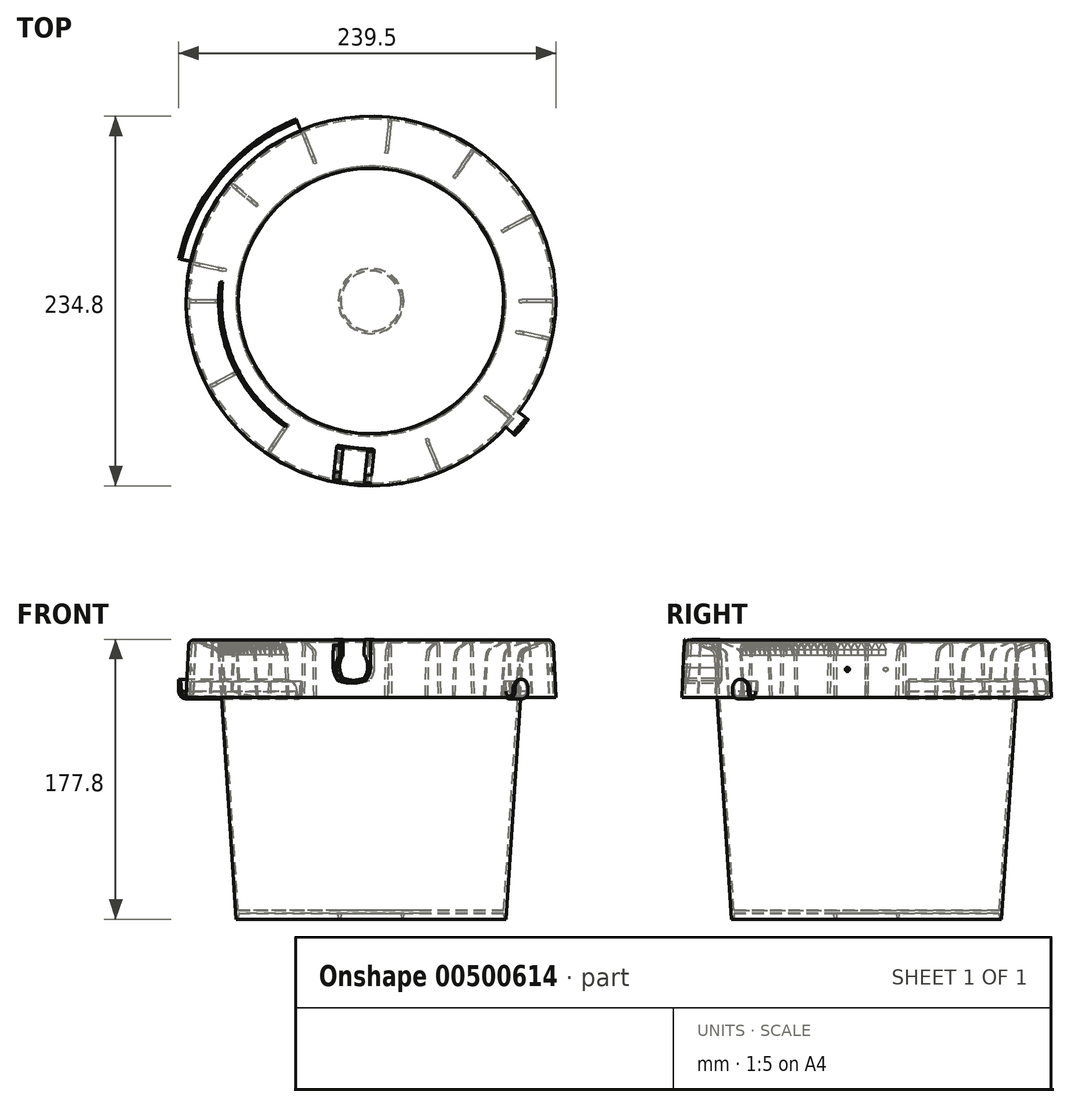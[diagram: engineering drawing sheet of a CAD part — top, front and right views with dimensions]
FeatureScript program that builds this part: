
annotation { "Feature Type Name" : "Feature", "Feature Type Description" : "" }
export const myFeature = defineFeature(function(context is Context, id is Id, definition is map)
    precondition{}
    {
        {
            var Q0;
            Q0=qCreatedBy(makeId("Front.planeOp"),FACE);
            var sketch = newSketch(context, id + "F0", { "sketchPlane" : qUnion([Q0])});
            skLineSegment(sketch, "E0", {"start": v(20.57, 0) * mm, "end": v(19.3, 0) * mm});
            skLineSegment(sketch, "E1", {"start": v(19.3, 0) * mm, "end": v(19.05, 3.81) * mm});
            skLineSegment(sketch, "E2", {"start": v(20.83, 3.81) * mm, "end": v(20.57, 0) * mm});
            skLineSegment(sketch, "E3", {"start": v(0, 0) * mm, "end": v(0, 3.81) * mm});
            skLineSegment(sketch, "E4", {"start": v(0, 3.81) * mm, "end": v(19.05, 3.81) * mm});
            skLineSegment(sketch, "E5", {"start": v(0, 3.81) * mm, "end": v(0, 5.59) * mm});
            skLineSegment(sketch, "E6", {"start": v(0, 5.59) * mm, "end": v(84.3, 5.59) * mm});
            skLineSegment(sketch, "E7", {"start": v(20.83, 3.81) * mm, "end": v(84.3, 3.8) * mm});
            skLineSegment(sketch, "E8", {"start": v(0, 0) * mm, "end": v(0, 179.07) * mm});
            skLineSegment(sketch, "E9", {"start": v(0, 0) * mm, "end": v(0, 171.45) * mm});
            skLineSegment(sketch, "E10", {"start": v(115.62, 140.97) * mm, "end": v(117.4, 140.97) * mm});
            skArc(sketch, "E11", {"start": v(114.08, 174.01) * mm, "mid": v(113.25, 175.47) * mm, "end": v(111.59, 175.66) * mm});
            skLineSegment(sketch, "E12", {"start": v(114.08, 174.01) * mm, "end": v(115.62, 140.97) * mm});
            skLineSegment(sketch, "E13", {"start": v(111.59, 175.66) * mm, "end": v(110.96, 177.33) * mm});
            skLineSegment(sketch, "E14", {"start": v(114.08, 174.01) * mm, "end": v(115.86, 174.1) * mm});
            skLineSegment(sketch, "E15", {"start": v(115.86, 174.1) * mm, "end": v(117.4, 140.97) * mm});
            skArc(sketch, "E16", {"start": v(99.32, 171.08) * mm, "mid": v(97.55, 169.74) * mm, "end": v(96.78, 167.65) * mm});
            skLineSegment(sketch, "E17", {"start": v(96.78, 167.65) * mm, "end": v(85.73, 0) * mm});
            skLineSegment(sketch, "E18", {"start": v(99.32, 171.08) * mm, "end": v(111.59, 175.66) * mm});
            skLineSegment(sketch, "E19", {"start": v(96.78, 167.65) * mm, "end": v(95, 167.77) * mm});
            skLineSegment(sketch, "E20", {"start": v(99.32, 171.08) * mm, "end": v(98.7, 172.74) * mm});
            skLineSegment(sketch, "E21", {"start": v(110.96, 177.33) * mm, "end": v(98.7, 172.74) * mm});
            skLineSegment(sketch, "E22", {"start": v(95, 167.77) * mm, "end": v(84.3, 5.59) * mm});
            skArc(sketch, "E23", {"start": v(98.7, 172.74) * mm, "mid": v(96.12, 170.8) * mm, "end": v(95, 167.77) * mm});
            skLineSegment(sketch, "E24", {"start": v(84.3, 3.8) * mm, "end": v(84.18, 3.8) * mm, "construction": true});
            skLineSegment(sketch, "E25", {"start": v(85.73, 0) * mm, "end": v(84.38, 0) * mm});
            skLineSegment(sketch, "E26", {"start": v(84.18, 3.8) * mm, "end": v(84.38, 0) * mm});
            skLineSegment(sketch, "E27", {"start": v(117.4, 140.97) * mm, "end": v(0, 140.97) * mm, "construction": true});
            skLineSegment(sketch, "E28", {"start": v(95, 167.77) * mm, "end": v(0, 167.77) * mm, "construction": true});
            skLineSegment(sketch, "E29", {"start": v(0, 177.33) * mm, "end": v(0, 179.1) * mm});
            skLineSegment(sketch, "E30", {"start": v(116.18, 167.13) * mm, "end": v(117.96, 167.13) * mm, "construction": true});
            skLineSegment(sketch, "E31", {"start": v(116.18, 167.13) * mm, "end": v(117.96, 167.13) * mm});
            skPoint(sketch, "E32.orphan", {"position": v(120.3, 167.13) * mm});
            skPoint(sketch, "E33.orphan", {"position": v(115.62, 167.13) * mm});
            skLineSegment(sketch, "E34", {"start": v(117.63, 174.1) * mm, "end": v(117.96, 167.13) * mm, "construction": true});
            skLineSegment(sketch, "E35", {"start": v(117.96, 167.13) * mm, "end": v(117.63, 174.1) * mm});
            skPoint(sketch, "E36.start.orphan", {"position": v(115.7, 177.55) * mm});
            skArc(sketch, "E37", {"start": v(117.63, 174.1) * mm, "mid": v(115.95, 177.7) * mm, "end": v(112.23, 179.07) * mm});
            skArc(sketch, "E38", {"start": v(115.86, 174.1) * mm, "mid": v(114.23, 176.96) * mm, "end": v(110.96, 177.33) * mm});
            skSolve(sketch);
        }
        {
            var Q0;
            Q0=qSketchRegion(id+"F0",true);
            var Q1;
            Q1=sQuery(id+"F0.wireOp",EDGE,"E9");
            revolve(context, id + "F1", {"entities" : qUnion([Q0]), "axis" : qUnion([Q1]), "revolveType" : RevolveType.FULL});
        }
        {
            var Q0;
            Q0=qCreatedBy(makeId("Front.planeOp"),FACE);
            var sketch = newSketch(context, id + "F2", { "sketchPlane" : qUnion([Q0])});
            skLineSegment(sketch, "E39", {"start": v(0, 0) * mm, "end": v(0, 3.8) * mm});
            skLineSegment(sketch, "E40", {"start": v(0, 3.8) * mm, "end": v(0, 5.59) * mm});
            skLineSegment(sketch, "E41", {"start": v(0, 0) * mm, "end": v(0, 179.07) * mm});
            skLineSegment(sketch, "E42", {"start": v(0, 0) * mm, "end": v(0, 171.45) * mm});
            skLineSegment(sketch, "E43", {"start": v(0, 179.07) * mm, "end": v(157.98, 179.07) * mm, "construction": true});
            skLineSegment(sketch, "E44", {"start": v(0, 179.07) * mm, "end": v(115.62, 179.07) * mm, "construction": true});
            skLineSegment(sketch, "E45", {"start": v(114.08, 174.01) * mm, "end": v(115.62, 140.97) * mm});
            skLineSegment(sketch, "E46", {"start": v(0, 177.55) * mm, "end": v(129.4, 177.55) * mm, "construction": true});
            skLineSegment(sketch, "E47", {"start": v(111.31, 176.37) * mm, "end": v(99.06, 171.79) * mm});
            skLineSegment(sketch, "E48", {"start": v(94.26, 140.97) * mm, "end": v(96.02, 167.65) * mm});
            skArc(sketch, "E49", {"start": v(99.06, 171.79) * mm, "mid": v(96.93, 170.16) * mm, "end": v(96.02, 167.65) * mm});
            skArc(sketch, "E50", {"start": v(114.08, 174.01) * mm, "mid": v(113.2, 175.8) * mm, "end": v(111.31, 176.37) * mm});
            skLineSegment(sketch, "E51", {"start": v(115.62, 140.97) * mm, "end": v(94.26, 140.97) * mm});
            skSolve(sketch);
        }
        {
            var Q0;
            Q0=makeQuery(id+"F2.imprint","IMPRINT",FACE,{"disambiguationData":[TD([[makeQuery(id+"F2.imprint","IMPRINT",EDGE,{"derivedFrom":sQuery(id+"F2.wireOp",EDGE,"E45")}),-1.0]])]});
            extrude(context, id + "F3", {"entities" : qUnion([Q0]), "endBound" : BoundingType.SYMMETRIC, "depth" : 1.78 * mm});
        }
        {
            var Q0;
            Q0=makeQuery(id+"F3.opExtrude","SWEPT_BODY",BODY,{"disambiguationData":[OSD([sQuery(id+"F2.wireOp",EDGE,"E45"),sQuery(id+"F2.wireOp",EDGE,"E47"),sQuery(id+"F2.wireOp",EDGE,"E48"),sQuery(id+"F2.wireOp",EDGE,"E49"),sQuery(id+"F2.wireOp",EDGE,"E50"),sQuery(id+"F2.wireOp",EDGE,"E51")])]});
            var Q1;
            Q1=makeQuery(id+"F1.opRevolve","SWEPT_FACE",FACE,{"disambiguationData":[OSD([sQuery(id+"F0.wireOp",EDGE,"E15")])]});
            circularPattern(context, id + "F4", {"entities" : qUnion([Q0]), "axis" : qUnion([Q1]), "angle" : 12 * degree, "instanceCount" : 2, "equalSpace" : true});
        }
        {
            var Q0;
            Q0=makeQuery(id+"F3.opExtrude","SWEPT_BODY",BODY,{"disambiguationData":[OSD([sQuery(id+"F2.wireOp",EDGE,"E45"),sQuery(id+"F2.wireOp",EDGE,"E47"),sQuery(id+"F2.wireOp",EDGE,"E48"),sQuery(id+"F2.wireOp",EDGE,"E49"),sQuery(id+"F2.wireOp",EDGE,"E50"),sQuery(id+"F2.wireOp",EDGE,"E51")])]});
            var Q1;
            Q1=makeQuery(id+"F1.opRevolve","SWEPT_FACE",FACE,{"disambiguationData":[OSD([sQuery(id+"F0.wireOp",EDGE,"E12")])]});
            circularPattern(context, id + "F5", {"entities" : qUnion([Q0]), "axis" : qUnion([Q1]), "angle" : 28 * degree, "instanceCount" : 2, "equalSpace" : true});
        }
        {
            var Q0;
            Q0=makeQuery(id+"F3.opExtrude","SWEPT_BODY",BODY,{"disambiguationData":[OSD([sQuery(id+"F2.wireOp",EDGE,"E45"),sQuery(id+"F2.wireOp",EDGE,"E47"),sQuery(id+"F2.wireOp",EDGE,"E48"),sQuery(id+"F2.wireOp",EDGE,"E49"),sQuery(id+"F2.wireOp",EDGE,"E50"),sQuery(id+"F2.wireOp",EDGE,"E51")])]});
            var Q1;
            Q1=makeQuery(id+"F1.opRevolve","SWEPT_FACE",FACE,{"disambiguationData":[OSD([sQuery(id+"F0.wireOp",EDGE,"E12")])]});
            circularPattern(context, id + "F6", {"entities" : qUnion([Q0]), "axis" : qUnion([Q1]), "angle" : 56 * degree, "instanceCount" : 2, "equalSpace" : true});
        }
        {
            var Q0;
            Q0=makeQuery(id+"F3.opExtrude","SWEPT_BODY",BODY,{"disambiguationData":[OSD([sQuery(id+"F2.wireOp",EDGE,"E45"),sQuery(id+"F2.wireOp",EDGE,"E47"),sQuery(id+"F2.wireOp",EDGE,"E48"),sQuery(id+"F2.wireOp",EDGE,"E49"),sQuery(id+"F2.wireOp",EDGE,"E50"),sQuery(id+"F2.wireOp",EDGE,"E51")])]});
            var Q1;
            Q1=makeQuery(id+"F1.opRevolve","SWEPT_FACE",FACE,{"disambiguationData":[OSD([sQuery(id+"F0.wireOp",EDGE,"E12")])]});
            circularPattern(context, id + "F7", {"entities" : qUnion([Q0]), "axis" : qUnion([Q1]), "angle" : 84 * degree, "instanceCount" : 2, "equalSpace" : true});
        }
        {
            var Q0;
            Q0=makeQuery(id+"F1.opRevolve","SWEPT_BODY",BODY,{"disambiguationData":[OSD([sQuery(id+"F0.wireOp",EDGE,"E0"),sQuery(id+"F0.wireOp",EDGE,"E1"),sQuery(id+"F0.wireOp",EDGE,"E2"),sQuery(id+"F0.wireOp",EDGE,"E4"),sQuery(id+"F0.wireOp",EDGE,"E6"),sQuery(id+"F0.wireOp",EDGE,"E7"),sQuery(id+"F0.wireOp",EDGE,"E9"),sQuery(id+"F0.wireOp",EDGE,"E10"),sQuery(id+"F0.wireOp",EDGE,"E11"),sQuery(id+"F0.wireOp",EDGE,"E12"),sQuery(id+"F0.wireOp",EDGE,"E15"),sQuery(id+"F0.wireOp",EDGE,"LKbFe0pn-6IGS-4NvF-Y8YP-ZpA0iSk9hzCY"),sQuery(id+"F0.wireOp",EDGE,"E16"),sQuery(id+"F0.wireOp",EDGE,"E17"),sQuery(id+"F0.wireOp",EDGE,"E18"),sQuery(id+"F0.wireOp",EDGE,"E21"),sQuery(id+"F0.wireOp",EDGE,"E22"),sQuery(id+"F0.wireOp",EDGE,"E23"),sQuery(id+"F0.wireOp",EDGE,"E25"),sQuery(id+"F0.wireOp",EDGE,"E26")])]});
            var Q1;
            Q1=makeQuery(id+"F3.opExtrude","SWEPT_BODY",BODY,{"disambiguationData":[OSD([sQuery(id+"F2.wireOp",EDGE,"E45"),sQuery(id+"F2.wireOp",EDGE,"E47"),sQuery(id+"F2.wireOp",EDGE,"E48"),sQuery(id+"F2.wireOp",EDGE,"E49"),sQuery(id+"F2.wireOp",EDGE,"E50"),sQuery(id+"F2.wireOp",EDGE,"E51")])]});
            var Q2;
            Q2=makeQuery(id+"F1.opRevolve","SWEPT_FACE",FACE,{"disambiguationData":[OSD([sQuery(id+"F0.wireOp",EDGE,"E12")])]});
            circularPattern(context, id + "F8", {"entities" : qUnion([Q0, Q1]), "axis" : qUnion([Q2]), "angle" : 112 * degree, "instanceCount" : 2, "equalSpace" : true});
        }
        {
            var Q0;
            Q0=makeQuery(id+"F3.opExtrude","SWEPT_BODY",BODY,{"disambiguationData":[OSD([sQuery(id+"F2.wireOp",EDGE,"E45"),sQuery(id+"F2.wireOp",EDGE,"E47"),sQuery(id+"F2.wireOp",EDGE,"E48"),sQuery(id+"F2.wireOp",EDGE,"E49"),sQuery(id+"F2.wireOp",EDGE,"E50"),sQuery(id+"F2.wireOp",EDGE,"E51")])]});
            var Q1;
            Q1=makeQuery(id+"F8.opPattern","COPY",FACE,{"derivedFrom":makeQuery(id+"F1.opRevolve","SWEPT_FACE",FACE,{"disambiguationData":[OSD([sQuery(id+"F0.wireOp",EDGE,"E12")])]}),"instanceName":"1"});
            circularPattern(context, id + "F9", {"entities" : qUnion([Q0]), "axis" : qUnion([Q1]), "angle" : 140 * degree, "instanceCount" : 2, "equalSpace" : true});
        }
        {
            var Q0;
            Q0=makeQuery(id+"F3.opExtrude","SWEPT_BODY",BODY,{"disambiguationData":[OSD([sQuery(id+"F2.wireOp",EDGE,"E45"),sQuery(id+"F2.wireOp",EDGE,"E47"),sQuery(id+"F2.wireOp",EDGE,"E48"),sQuery(id+"F2.wireOp",EDGE,"E49"),sQuery(id+"F2.wireOp",EDGE,"E50"),sQuery(id+"F2.wireOp",EDGE,"E51")])]});
            var Q1;
            Q1=makeQuery(id+"F8.opPattern","COPY",FACE,{"derivedFrom":makeQuery(id+"F1.opRevolve","SWEPT_FACE",FACE,{"disambiguationData":[OSD([sQuery(id+"F0.wireOp",EDGE,"E12")])]}),"instanceName":"1"});
            circularPattern(context, id + "F10", {"entities" : qUnion([Q0]), "axis" : qUnion([Q1]), "angle" : 168 * degree, "instanceCount" : 2, "equalSpace" : true});
        }
        {
            var Q0;
            Q0=makeQuery(id+"F3.opExtrude","SWEPT_BODY",BODY,{"disambiguationData":[OSD([sQuery(id+"F2.wireOp",EDGE,"E45"),sQuery(id+"F2.wireOp",EDGE,"E47"),sQuery(id+"F2.wireOp",EDGE,"E48"),sQuery(id+"F2.wireOp",EDGE,"E49"),sQuery(id+"F2.wireOp",EDGE,"E50"),sQuery(id+"F2.wireOp",EDGE,"E51")])]});
            var Q1;
            Q1=makeQuery(id+"F1.opRevolve","SWEPT_FACE",FACE,{"disambiguationData":[OSD([sQuery(id+"F0.wireOp",EDGE,"E11")])]});
            circularPattern(context, id + "F11", {"entities" : qUnion([Q0]), "axis" : qUnion([Q1]), "angle" : 180 * degree, "instanceCount" : 2, "equalSpace" : true});
        }
        {
            var Q0;
            Q0=makeQuery(id+"F3.opExtrude","SWEPT_BODY",BODY,{"disambiguationData":[OSD([sQuery(id+"F2.wireOp",EDGE,"E45"),sQuery(id+"F2.wireOp",EDGE,"E47"),sQuery(id+"F2.wireOp",EDGE,"E48"),sQuery(id+"F2.wireOp",EDGE,"E49"),sQuery(id+"F2.wireOp",EDGE,"E50"),sQuery(id+"F2.wireOp",EDGE,"E51")])]});
            var Q1;
            Q1=makeQuery(id+"F8.opPattern","COPY",FACE,{"derivedFrom":makeQuery(id+"F1.opRevolve","SWEPT_FACE",FACE,{"disambiguationData":[OSD([sQuery(id+"F0.wireOp",EDGE,"E15")])]}),"instanceName":"1"});
            circularPattern(context, id + "F12", {"entities" : qUnion([Q0]), "axis" : qUnion([Q1]), "angle" : 208 * degree, "instanceCount" : 2, "oppositeDirection" : true, "equalSpace" : true});
        }
        {
            var Q0;
            Q0=makeQuery(id+"F3.opExtrude","SWEPT_BODY",BODY,{"disambiguationData":[OSD([sQuery(id+"F2.wireOp",EDGE,"E45"),sQuery(id+"F2.wireOp",EDGE,"E47"),sQuery(id+"F2.wireOp",EDGE,"E48"),sQuery(id+"F2.wireOp",EDGE,"E49"),sQuery(id+"F2.wireOp",EDGE,"E50"),sQuery(id+"F2.wireOp",EDGE,"E51")])]});
            var Q1;
            Q1=makeQuery(id+"F1.opRevolve","SWEPT_FACE",FACE,{"disambiguationData":[OSD([sQuery(id+"F0.wireOp",EDGE,"E15")])]});
            circularPattern(context, id + "F13", {"entities" : qUnion([Q0]), "axis" : qUnion([Q1]), "angle" : 236 * degree, "instanceCount" : 2, "oppositeDirection" : true, "equalSpace" : true});
        }
        {
            var Q0;
            Q0=makeQuery(id+"F3.opExtrude","SWEPT_BODY",BODY,{"disambiguationData":[OSD([sQuery(id+"F2.wireOp",EDGE,"E45"),sQuery(id+"F2.wireOp",EDGE,"E47"),sQuery(id+"F2.wireOp",EDGE,"E48"),sQuery(id+"F2.wireOp",EDGE,"E49"),sQuery(id+"F2.wireOp",EDGE,"E50"),sQuery(id+"F2.wireOp",EDGE,"E51")])]});
            var Q1;
            Q1=makeQuery(id+"F8.opPattern","COPY",FACE,{"derivedFrom":makeQuery(id+"F1.opRevolve","SWEPT_FACE",FACE,{"disambiguationData":[OSD([sQuery(id+"F0.wireOp",EDGE,"E12")])]}),"instanceName":"1"});
            circularPattern(context, id + "F14", {"entities" : qUnion([Q0]), "axis" : qUnion([Q1]), "angle" : 40 * degree, "instanceCount" : 2, "oppositeDirection" : true, "equalSpace" : true});
        }
        {
            var Q0;
            Q0=makeQuery(id+"F3.opExtrude","SWEPT_BODY",BODY,{"disambiguationData":[OSD([sQuery(id+"F2.wireOp",EDGE,"E45"),sQuery(id+"F2.wireOp",EDGE,"E47"),sQuery(id+"F2.wireOp",EDGE,"E48"),sQuery(id+"F2.wireOp",EDGE,"E49"),sQuery(id+"F2.wireOp",EDGE,"E50"),sQuery(id+"F2.wireOp",EDGE,"E51")])]});
            var Q1;
            Q1=makeQuery(id+"F1.opRevolve","SWEPT_FACE",FACE,{"disambiguationData":[OSD([sQuery(id+"F0.wireOp",EDGE,"E12")])]});
            circularPattern(context, id + "F15", {"entities" : qUnion([Q0]), "axis" : qUnion([Q1]), "angle" : 68 * degree, "instanceCount" : 2, "oppositeDirection" : true, "equalSpace" : true});
        }
        {
            var Q0;
            Q0=makeQuery(id+"F4.opPattern","COPY",FACE,{"derivedFrom":makeQuery(id+"F3.opExtrude","CAP_FACE",FACE,{"disambiguationData":[OSD([sQuery(id+"F2.wireOp",EDGE,"E45"),sQuery(id+"F2.wireOp",EDGE,"E47"),sQuery(id+"F2.wireOp",EDGE,"E48"),sQuery(id+"F2.wireOp",EDGE,"E49"),sQuery(id+"F2.wireOp",EDGE,"E50"),sQuery(id+"F2.wireOp",EDGE,"E51")])],"isStart":false}),"instanceName":"1"});
            var Q1;
            Q1=makeQuery(id+"F3.opExtrude","CAP_FACE",FACE,{"disambiguationData":[OSD([sQuery(id+"F2.wireOp",EDGE,"E45"),sQuery(id+"F2.wireOp",EDGE,"E47"),sQuery(id+"F2.wireOp",EDGE,"E48"),sQuery(id+"F2.wireOp",EDGE,"E49"),sQuery(id+"F2.wireOp",EDGE,"E50"),sQuery(id+"F2.wireOp",EDGE,"E51")])],"isStart":true});
            cPlane(context, id + "F16", {"entities" : qUnion([Q0, Q1]), "cplaneType" : CPlaneType.MID_PLANE, "offset" : 25.4 * mm, "width" : 152.4 * mm, "height" : 152.4 * mm});
        }
        {
            var Q0;
            Q0=qCreatedBy(id+"F16.planeOp",FACE);
            cPlane(context, id + "F17", {"entities" : qUnion([Q0]), "cplaneType" : CPlaneType.OFFSET, "offset" : 127 * mm, "width" : 152.4 * mm, "height" : 152.4 * mm});
        }
        {
            var Q0;
            Q0=makeQuery(id+"F7.opPattern","COPY",FACE,{"derivedFrom":makeQuery(id+"F3.opExtrude","CAP_FACE",FACE,{"disambiguationData":[OSD([sQuery(id+"F2.wireOp",EDGE,"E45"),sQuery(id+"F2.wireOp",EDGE,"E47"),sQuery(id+"F2.wireOp",EDGE,"E48"),sQuery(id+"F2.wireOp",EDGE,"E49"),sQuery(id+"F2.wireOp",EDGE,"E50"),sQuery(id+"F2.wireOp",EDGE,"E51")])],"isStart":false}),"instanceName":"1"});
            cPlane(context, id + "F18", {"entities" : qUnion([Q0]), "cplaneType" : CPlaneType.OFFSET, "offset" : 0.89 * mm, "oppositeDirection" : true, "width" : 152.4 * mm, "height" : 152.4 * mm});
        }
        {
            var Q0;
            Q0=qCreatedBy(id+"F18.planeOp",FACE);
            cPlane(context, id + "F19", {"entities" : qUnion([Q0]), "cplaneType" : CPlaneType.OFFSET, "offset" : 127 * mm, "width" : 152.4 * mm, "height" : 152.4 * mm});
        }
        {
            var Q0;
            Q0=qCreatedBy(id+"F19.planeOp",FACE);
            var sketch = newSketch(context, id + "F20", { "sketchPlane" : qUnion([Q0])});
            skLineSegment(sketch, "E52", {"start": v(0, 0) * mm, "end": v(0, 158.75) * mm, "construction": true});
            skCircle(sketch, "E53", {"center": v(0, 158.75) * mm, "radius": 1.27 * mm});
            skSolve(sketch);
        }
        {
            var Q0;
            Q0=makeQuery(id+"F20.imprint","IMPRINT",FACE,{"disambiguationData":[TD([[makeQuery(id+"F20.imprint","IMPRINT",EDGE,{"derivedFrom":sQuery(id+"F20.wireOp",EDGE,"E53")}),1.0]])]});
            extrude(context, id + "F21", {"entities" : qUnion([Q0]), "operationType" : NewBodyOperationType.REMOVE, "oppositeDirection" : true, "depth" : 25.4 * mm});
        }
        {
            var Q0;
            Q0=qCreatedBy(id+"F19.planeOp",FACE);
            cPlane(context, id + "F22", {"entities" : qUnion([Q0]), "cplaneType" : CPlaneType.OFFSET, "offset" : 254 * mm, "oppositeDirection" : true, "width" : 152.4 * mm, "height" : 152.4 * mm});
        }
        {
            var Q0;
            Q0=qCreatedBy(id+"F22.planeOp",FACE);
            var sketch = newSketch(context, id + "F23", { "sketchPlane" : qUnion([Q0])});
            skLineSegment(sketch, "E54", {"start": v(0, 0) * mm, "end": v(0, 158.75) * mm, "construction": true});
            skCircle(sketch, "E55", {"center": v(0, 158.75) * mm, "radius": 1.27 * mm});
            skSolve(sketch);
        }
        {
            var Q0;
            Q0=makeQuery(id+"F23.imprint","IMPRINT",FACE,{"disambiguationData":[TD([[makeQuery(id+"F23.imprint","IMPRINT",EDGE,{"derivedFrom":sQuery(id+"F23.wireOp",EDGE,"E55")}),1.0]])]});
            extrude(context, id + "F24", {"entities" : qUnion([Q0]), "operationType" : NewBodyOperationType.REMOVE, "depth" : 25.4 * mm});
        }
        {
            var Q0;
            Q0=qCreatedBy(id+"F17.planeOp",FACE);
            cPlane(context, id + "F25", {"entities" : qUnion([Q0]), "cplaneType" : CPlaneType.OFFSET, "offset" : 25.4 * mm, "oppositeDirection" : true, "width" : 152.4 * mm, "height" : 152.4 * mm});
        }
        {
            var Q0;
            Q0=qCreatedBy(id+"F16.planeOp",FACE);
            var sketch = newSketch(context, id + "F26", { "sketchPlane" : qUnion([Q0])});
            skLineSegment(sketch, "E56", {"start": v(0, 0) * mm, "end": v(-95, 0) * mm, "construction": true});
            skLineSegment(sketch, "E57", {"start": v(-95, 0) * mm, "end": v(-95, 167.77) * mm, "construction": true});
            skLineSegment(sketch, "E58", {"start": v(-95, 167.77) * mm, "end": v(-95, 176.02) * mm});
            skLineSegment(sketch, "E59", {"start": v(-95, 176.02) * mm, "end": v(-96.77, 176.02) * mm});
            skLineSegment(sketch, "E60", {"start": v(-96.77, 176.02) * mm, "end": v(-96.77, 171.3) * mm});
            skLineSegment(sketch, "E61", {"start": v(-95, 167.77) * mm, "end": v(-96.77, 171.3) * mm});
            skSolve(sketch);
        }
        {
            var Q0;
            Q0=makeQuery(id+"F26.imprint","IMPRINT",FACE,{"disambiguationData":[TD([[makeQuery(id+"F26.imprint","IMPRINT",EDGE,{"derivedFrom":sQuery(id+"F26.wireOp",EDGE,"E58")}),1.0]])]});
            extrude(context, id + "F27", {"entities" : qUnion([Q0]), "depth" : 2.22 * mm, "hasSecondDirection" : true, "secondDirectionOppositeDirection" : true, "secondDirectionDepth" : 2.22 * mm});
        }
        {
            var Q0;
            Q0=makeQuery(id+"F27.opExtrude","SWEPT_FACE",FACE,{"disambiguationData":[OSD([sQuery(id+"F26.wireOp",EDGE,"E60")])]});
            var sketch = newSketch(context, id + "F28", { "sketchPlane" : qUnion([Q0])});
            skLineSegment(sketch, "E62", {"start": v(2.22, 176.02) * mm, "end": v(2.22, 171.63) * mm});
            skLineSegment(sketch, "E63", {"start": v(2.22, 171.63) * mm, "end": v(0, 176.02) * mm});
            skLineSegment(sketch, "E64", {"start": v(0, 176.02) * mm, "end": v(2.22, 176.02) * mm});
            skSolve(sketch);
        }
        {
            var Q0;
            Q0=makeQuery(id+"F28.imprint","IMPRINT",FACE,{"disambiguationData":[TD([[makeQuery(id+"F28.imprint","IMPRINT",EDGE,{"derivedFrom":sQuery(id+"F28.wireOp",EDGE,"E62")}),-1.0]])]});
            extrude(context, id + "F29", {"entities" : qUnion([Q0]), "operationType" : NewBodyOperationType.REMOVE, "oppositeDirection" : true, "depth" : 25.4 * mm});
        }
        {
            var Q0;
            Q0=makeQuery(id+"F27.opExtrude","SWEPT_FACE",FACE,{"disambiguationData":[OSD([sQuery(id+"F26.wireOp",EDGE,"E60")])]});
            var sketch = newSketch(context, id + "F30", { "sketchPlane" : qUnion([Q0])});
            skLineSegment(sketch, "E65", {"start": v(0, 176.02) * mm, "end": v(-2.22, 176.02) * mm});
            skLineSegment(sketch, "E66", {"start": v(-2.22, 176.02) * mm, "end": v(-2.22, 171.64) * mm});
            skLineSegment(sketch, "E67", {"start": v(-2.22, 171.64) * mm, "end": v(0, 176.02) * mm});
            skSolve(sketch);
        }
        {
            var Q0;
            Q0=makeQuery(id+"F30.imprint","IMPRINT",FACE,{"disambiguationData":[TD([[makeQuery(id+"F30.imprint","IMPRINT",EDGE,{"derivedFrom":sQuery(id+"F30.wireOp",EDGE,"E65")}),1.0]])]});
            extrude(context, id + "F31", {"entities" : qUnion([Q0]), "operationType" : NewBodyOperationType.REMOVE, "oppositeDirection" : true, "depth" : 25.4 * mm});
        }
        {
            var Q0;
            Q0=makeQuery(id+"F27.opExtrude","SWEPT_BODY",BODY,{"disambiguationData":[OSD([sQuery(id+"F26.wireOp",EDGE,"E58"),sQuery(id+"F26.wireOp",EDGE,"E59"),sQuery(id+"F26.wireOp",EDGE,"E60"),sQuery(id+"F26.wireOp",EDGE,"E61")])]});
            var Q1;
            Q1=makeQuery(id+"F1.opRevolve","SWEPT_FACE",FACE,{"disambiguationData":[OSD([sQuery(id+"F0.wireOp",EDGE,"E22")])]});
            circularPattern(context, id + "F32", {"entities" : qUnion([Q0]), "axis" : qUnion([Q1]), "angle" : 60.5 * degree, "instanceCount" : 24, "oppositeDirection" : true, "equalSpace" : true});
        }
        {
            var Q0;
            Q0=makeQuery(id+"F10.opPattern","COPY",FACE,{"derivedFrom":makeQuery(id+"F3.opExtrude","CAP_FACE",FACE,{"disambiguationData":[OSD([sQuery(id+"F2.wireOp",EDGE,"E45"),sQuery(id+"F2.wireOp",EDGE,"E47"),sQuery(id+"F2.wireOp",EDGE,"E48"),sQuery(id+"F2.wireOp",EDGE,"E49"),sQuery(id+"F2.wireOp",EDGE,"E50"),sQuery(id+"F2.wireOp",EDGE,"E51")])],"isStart":false}),"instanceName":"1"});
            var sketch = newSketch(context, id + "F33", { "sketchPlane" : qUnion([Q0])});
            skLineSegment(sketch, "E68", {"start": v(115.5, 140.97) * mm, "end": v(115.05, 151.12) * mm});
            skLineSegment(sketch, "E69", {"start": v(117.3, 151.12) * mm, "end": v(118.28, 141.1) * mm});
            skLineSegment(sketch, "E70", {"start": v(117.3, 151.12) * mm, "end": v(115.05, 151.12) * mm});
            skLineSegment(sketch, "E71", {"start": v(118.28, 141.1) * mm, "end": v(118.46, 139.23) * mm});
            skLineSegment(sketch, "E72", {"start": v(115.5, 140.97) * mm, "end": v(115.5, 139.25) * mm});
            skLineSegment(sketch, "E73", {"start": v(115.5, 139.25) * mm, "end": v(118.46, 139.23) * mm});
            skSolve(sketch);
        }
        {
            var Q0;
            {var subQ2=sQuery(id+"F33.wireOp",EDGE,"E69");Q0=makeQuery(id+"F33.imprint","IMPRINT",FACE,{"disambiguationData":[TD([[makeQuery(id+"F33.imprint","IMPRINT",EDGE,{"derivedFrom":subQ2}),-1.0]])]});}
            var Q1;
            Q1=makeQuery(id+"F8.opPattern","COPY",FACE,{"derivedFrom":makeQuery(id+"F1.opRevolve","SWEPT_FACE",FACE,{"disambiguationData":[OSD([sQuery(id+"F0.wireOp",EDGE,"E15")])]}),"instanceName":"1"});
            revolve(context, id + "F34", {"operationType" : NewBodyOperationType.REMOVE, "entities" : qUnion([Q0]), "axis" : qUnion([Q1]), "revolveType" : RevolveType.ONE_DIRECTION, "angle" : 55 * degree});
        }
        {
            var Q0;
            {var subQ0=sQuery(id+"F33.wireOp",EDGE,"E70");Q0=makeQuery(id+"F34.boolean.opBoolean","COPY",FACE,{"disambiguationData":[TD([makeQuery(id+"F8.opPattern","COPY",FACE,{"derivedFrom":makeQuery(id+"F1.opRevolve","SWEPT_FACE",FACE,{"disambiguationData":[OSD([sQuery(id+"F0.wireOp",EDGE,"E10")])]}),"instanceName":"1"})])],"derivedFrom":makeQuery(id+"F34.opRevolve","CAP_FACE",FACE,{"disambiguationData":[OSD([sQuery(id+"F2.wireOp",EDGE,"E45"),sQuery(id+"F2.wireOp",EDGE,"E51"),sQuery(id+"F33.wireOp",EDGE,"E69"),subQ0,sQuery(id+"F33.wireOp",EDGE,"E71"),sQuery(id+"F33.wireOp",EDGE,"E72"),sQuery(id+"F33.wireOp",EDGE,"E73")])],"isStart":true})});}
            var sketch = newSketch(context, id + "F35", { "sketchPlane" : qUnion([Q0])});
            skLineSegment(sketch, "E74", {"start": v(115.62, 140.97) * mm, "end": v(125.02, 140.97) * mm, "construction": true});
            skLineSegment(sketch, "E75", {"start": v(115.62, 140.97) * mm, "end": v(120.32, 140.97) * mm, "construction": true});
            skLineSegment(sketch, "E76", {"start": v(116.92, 151.12) * mm, "end": v(115.15, 151.12) * mm});
            skLineSegment(sketch, "E77", {"start": v(115.15, 151.12) * mm, "end": v(115.44, 144.83) * mm});
            skLineSegment(sketch, "E78", {"start": v(115.44, 144.83) * mm, "end": v(115.44, 144.83) * mm});
            skArc(sketch, "E79", {"start": v(115.44, 144.83) * mm, "mid": v(120.23, 140.04) * mm, "end": v(125.02, 144.83) * mm});
            skLineSegment(sketch, "E80", {"start": v(125.02, 152.45) * mm, "end": v(123.75, 152.45) * mm});
            skLineSegment(sketch, "E81", {"start": v(123.75, 152.45) * mm, "end": v(123.24, 144.83) * mm});
            skLineSegment(sketch, "E82", {"start": v(120.23, 140.97) * mm, "end": v(120.23, 141.82) * mm});
            skArc(sketch, "E83", {"start": v(117.22, 144.83) * mm, "mid": v(120.23, 141.82) * mm, "end": v(123.24, 144.83) * mm});
            skLineSegment(sketch, "E84", {"start": v(116.92, 151.12) * mm, "end": v(117.22, 144.83) * mm});
            skPoint(sketch, "E85.orphan", {"position": v(120.23, 140.04) * mm});
            skLineSegment(sketch, "E86", {"start": v(125.02, 152.45) * mm, "end": v(125.02, 144.83) * mm});
            skLineSegment(sketch, "E87", {"start": v(0, 0) * mm, "end": v(0, 224.67) * mm, "construction": true});
            skLineSegment(sketch, "E88", {"start": v(115.44, 144.83) * mm, "end": v(0, 144.83) * mm, "construction": true});
            skLineSegment(sketch, "E89", {"start": v(0, 144.83) * mm, "end": v(-115.44, 144.83) * mm, "construction": true});
            skSolve(sketch);
        }
        {
            var Q0;
            Q0=makeQuery(id+"F35.imprint","IMPRINT",FACE,{"disambiguationData":[TD([[makeQuery(id+"F35.imprint","IMPRINT",EDGE,{"derivedFrom":sQuery(id+"F35.wireOp",EDGE,"E80")}),1.0]])]});
            var Q1;
            Q1=makeQuery(id+"F35.imprint","IMPRINT",FACE,{"disambiguationData":[TD([[makeQuery(id+"F35.imprint","IMPRINT",EDGE,{"derivedFrom":sQuery(id+"F35.wireOp",EDGE,"E76")}),1.0]])]});
            var Q2;
            Q2=makeQuery(id+"F1.opRevolve","SWEPT_FACE",FACE,{"disambiguationData":[OSD([sQuery(id+"F0.wireOp",EDGE,"E15")])]});
            revolve(context, id + "F36", {"entities" : qUnion([Q0, Q1]), "axis" : qUnion([Q2]), "revolveType" : RevolveType.ONE_DIRECTION, "angle" : 55.2 * degree});
        }
        {
            var Q0;
            Q0=makeQuery(id+"F36.opRevolve","CAP_EDGE",EDGE,{"disambiguationData":[OSD([sQuery(id+"F35.wireOp",EDGE,"E80")]),OD(0.0)],"isStart":false});
            var Q1;
            Q1=makeQuery(id+"F36.opRevolve","CAP_EDGE",EDGE,{"disambiguationData":[OSD([sQuery(id+"F35.wireOp",EDGE,"E80")]),OD(1.0)],"isStart":false});
            fillet(context, id + "F37", {"entities" : qUnion([Q0, Q1]), "radius" : 7.62 * mm, "tangentPropagation" : true, "allowEdgeOverflow" : false});
        }
        {
            var Q0;
            Q0=makeQuery(id+"F9.opPattern","COPY",FACE,{"derivedFrom":makeQuery(id+"F3.opExtrude","CAP_FACE",FACE,{"disambiguationData":[OSD([sQuery(id+"F2.wireOp",EDGE,"E45"),sQuery(id+"F2.wireOp",EDGE,"E47"),sQuery(id+"F2.wireOp",EDGE,"E48"),sQuery(id+"F2.wireOp",EDGE,"E49"),sQuery(id+"F2.wireOp",EDGE,"E50"),sQuery(id+"F2.wireOp",EDGE,"E51")])],"isStart":true}),"instanceName":"1"});
            var sketch = newSketch(context, id + "F38", { "sketchPlane" : qUnion([Q0])});
            skLineSegment(sketch, "E90", {"start": v(-115.36, 144.6) * mm, "end": v(-115.62, 140.97) * mm});
            skLineSegment(sketch, "E91", {"start": v(-115.62, 140.97) * mm, "end": v(-94.98, 140.97) * mm});
            skLineSegment(sketch, "E92", {"start": v(-94.98, 140.97) * mm, "end": v(-115.36, 144.6) * mm});
            skSolve(sketch);
        }
        {
            var Q0;
            Q0=makeQuery(id+"F38.imprint","IMPRINT",FACE,{"disambiguationData":[TD([[makeQuery(id+"F38.imprint","IMPRINT",EDGE,{"derivedFrom":sQuery(id+"F38.wireOp",EDGE,"E90")}),1.0]])]});
            extrude(context, id + "F39", {"entities" : qUnion([Q0]), "operationType" : NewBodyOperationType.REMOVE, "oppositeDirection" : true, "depth" : 1.78 * mm});
        }
        {
            var Q0;
            Q0=makeQuery(id+"F9.opPattern","COPY",FACE,{"derivedFrom":makeQuery(id+"F3.opExtrude","CAP_FACE",FACE,{"disambiguationData":[OSD([sQuery(id+"F2.wireOp",EDGE,"E45"),sQuery(id+"F2.wireOp",EDGE,"E47"),sQuery(id+"F2.wireOp",EDGE,"E48"),sQuery(id+"F2.wireOp",EDGE,"E49"),sQuery(id+"F2.wireOp",EDGE,"E50"),sQuery(id+"F2.wireOp",EDGE,"E51")])],"isStart":true}),"instanceName":"1"});
            var sketch = newSketch(context, id + "F40", { "sketchPlane" : qUnion([Q0])});
            skLineSegment(sketch, "E93", {"start": v(-115.62, 140.97) * mm, "end": v(-115.36, 144.6) * mm});
            skLineSegment(sketch, "E94", {"start": v(-115.62, 140.97) * mm, "end": v(-115.45, 144.61) * mm});
            skLineSegment(sketch, "E95", {"start": v(-115.45, 144.61) * mm, "end": v(-115.36, 144.6) * mm});
            skSolve(sketch);
        }
        {
            var Q0;
            Q0=makeQuery(id+"F40.imprint","IMPRINT",FACE,{"disambiguationData":[TD([[makeQuery(id+"F40.imprint","IMPRINT",EDGE,{"derivedFrom":sQuery(id+"F40.wireOp",EDGE,"E93")}),-1.0]])]});
            extrude(context, id + "F41", {"entities" : qUnion([Q0]), "operationType" : NewBodyOperationType.REMOVE, "oppositeDirection" : true, "depth" : 1.78 * mm});
        }
        {
            var Q0;
            {var subQ0=sQuery(id+"F33.wireOp",EDGE,"E70");Q0=makeQuery(id+"F34.boolean.opBoolean","COPY",FACE,{"disambiguationData":[TD([makeQuery(id+"F8.opPattern","COPY",FACE,{"derivedFrom":makeQuery(id+"F1.opRevolve","SWEPT_FACE",FACE,{"disambiguationData":[OSD([sQuery(id+"F0.wireOp",EDGE,"E10")])]}),"instanceName":"1"})])],"derivedFrom":makeQuery(id+"F34.opRevolve","CAP_FACE",FACE,{"disambiguationData":[OSD([sQuery(id+"F2.wireOp",EDGE,"E45"),sQuery(id+"F2.wireOp",EDGE,"E51"),sQuery(id+"F33.wireOp",EDGE,"E69"),subQ0,sQuery(id+"F33.wireOp",EDGE,"E71"),sQuery(id+"F33.wireOp",EDGE,"E72"),sQuery(id+"F33.wireOp",EDGE,"E73")])],"isStart":false})});}
            var sketch = newSketch(context, id + "F42", { "sketchPlane" : qUnion([Q0])});
            skLineSegment(sketch, "E96", {"start": v(-115.62, 140.97) * mm, "end": v(-117.38, 140.97) * mm});
            skLineSegment(sketch, "E97", {"start": v(-115.62, 140.97) * mm, "end": v(-115.47, 144.2) * mm});
            skArc(sketch, "E98", {"start": v(-117.38, 140.97) * mm, "mid": v(-116.1, 142.39) * mm, "end": v(-115.47, 144.2) * mm});
            skSolve(sketch);
        }
        {
            var Q0;
            Q0=makeQuery(id+"F42.imprint","IMPRINT",FACE,{"disambiguationData":[TD([[makeQuery(id+"F42.imprint","IMPRINT",EDGE,{"derivedFrom":sQuery(id+"F42.wireOp",EDGE,"E96")}),1.0]])]});
            extrude(context, id + "F43", {"entities" : qUnion([Q0]), "operationType" : NewBodyOperationType.REMOVE, "oppositeDirection" : true, "depth" : 0.24 * mm});
        }
        {
            var Q0;
            Q0=qCreatedBy(id+"F25.planeOp",FACE);
            cPlane(context, id + "F44", {"entities" : qUnion([Q0]), "cplaneType" : CPlaneType.OFFSET, "offset" : 25.4 * mm, "width" : 152.4 * mm, "height" : 152.4 * mm});
        }
        {
            var Q0;
            Q0=qCreatedBy(id+"F44.planeOp",FACE);
            var sketch = newSketch(context, id + "F45", { "sketchPlane" : qUnion([Q0])});
            skLineSegment(sketch, "E99", {"start": v(0, 0) * mm, "end": v(0, 151.77) * mm, "construction": true});
            skLineSegment(sketch, "E100", {"start": v(-7.87, 177.8) * mm, "end": v(-7.87, 167.64) * mm});
            skLineSegment(sketch, "E101", {"start": v(7.87, 167.64) * mm, "end": v(7.87, 177.8) * mm});
            skArc(sketch, "E102", {"start": v(-7.87, 167.64) * mm, "mid": v(-10.16, 160.4) * mm, "end": v(-7.87, 153.16) * mm});
            skArc(sketch, "E103", {"start": v(7.87, 153.16) * mm, "mid": v(10.16, 160.4) * mm, "end": v(7.87, 167.64) * mm});
            skArc(sketch, "E104", {"start": v(-7.87, 153.16) * mm, "mid": v(0, 151.77) * mm, "end": v(7.87, 153.16) * mm});
            skPoint(sketch, "E105.orphan", {"position": v(0, 167.64) * mm});
            skLineSegment(sketch, "E106", {"start": v(-7.87, 177.8) * mm, "end": v(7.87, 177.8) * mm});
            skPoint(sketch, "E107.start.orphan", {"position": v(0, 160.4) * mm});
            skArc(sketch, "E108.2", {"start": v(9, 151.69) * mm, "mid": v(11.27, 156.07) * mm, "end": v(11.93, 160.97) * mm});
            skArc(sketch, "E108.4", {"start": v(-9, 151.69) * mm, "mid": v(0, 149.99) * mm, "end": v(9, 151.69) * mm});
            skArc(sketch, "E108.5", {"start": v(-11.93, 160.97) * mm, "mid": v(-11.27, 156.07) * mm, "end": v(-9, 151.69) * mm});
            skLineSegment(sketch, "E109", {"start": v(11.93, 159.83) * mm, "end": v(11.93, 177.8) * mm});
            skLineSegment(sketch, "E110", {"start": v(-11.93, 159.83) * mm, "end": v(-11.93, 177.8) * mm});
            skLineSegment(sketch, "E111", {"start": v(-7.87, 177.8) * mm, "end": v(-11.93, 177.8) * mm});
            skLineSegment(sketch, "E112", {"start": v(7.87, 177.8) * mm, "end": v(11.93, 177.8) * mm});
            skSolve(sketch);
        }
        {
            var Q0;
            Q0=makeQuery(id+"F45.imprint","IMPRINT",FACE,{"disambiguationData":[TD([[makeQuery(id+"F45.imprint","IMPRINT",EDGE,{"derivedFrom":sQuery(id+"F45.wireOp",EDGE,"E100")}),1.0]])]});
            var Q1;
            Q1=makeQuery(id+"F45.imprint","IMPRINT",FACE,{"disambiguationData":[TD([[makeQuery(id+"F45.imprint","IMPRINT",EDGE,{"derivedFrom":sQuery(id+"F45.wireOp",EDGE,"E100")}),-1.0]])]});
            extrude(context, id + "F46", {"entities" : qUnion([Q0, Q1]), "operationType" : NewBodyOperationType.REMOVE, "oppositeDirection" : true, "depth" : 50.8 * mm});
        }
        {
            var Q0;
            Q0=qCreatedBy(id+"F25.planeOp",FACE);
            var sketch = newSketch(context, id + "F47", { "sketchPlane" : qUnion([Q0])});
            skLineSegment(sketch, "E113", {"start": v(0, 0) * mm, "end": v(0, 151.77) * mm, "construction": true});
            skLineSegment(sketch, "E114", {"start": v(-7.87, 177.8) * mm, "end": v(-7.87, 167.64) * mm});
            skLineSegment(sketch, "E115", {"start": v(7.87, 167.64) * mm, "end": v(7.87, 177.8) * mm});
            skArc(sketch, "E116", {"start": v(-7.87, 167.64) * mm, "mid": v(-10.16, 160.4) * mm, "end": v(-7.87, 153.16) * mm});
            skArc(sketch, "E117", {"start": v(7.87, 153.16) * mm, "mid": v(10.16, 160.4) * mm, "end": v(7.87, 167.64) * mm});
            skArc(sketch, "E118", {"start": v(-7.87, 153.16) * mm, "mid": v(0, 151.77) * mm, "end": v(7.87, 153.16) * mm});
            skPoint(sketch, "E119.orphan", {"position": v(0, 167.64) * mm});
            skLineSegment(sketch, "E120", {"start": v(-7.87, 177.8) * mm, "end": v(7.87, 177.8) * mm});
            skPoint(sketch, "E121.start.orphan", {"position": v(0, 160.4) * mm});
            skArc(sketch, "E122.2", {"start": v(9, 151.69) * mm, "mid": v(11.27, 156.07) * mm, "end": v(11.93, 160.97) * mm});
            skArc(sketch, "E122.4", {"start": v(-9, 151.69) * mm, "mid": v(0, 149.99) * mm, "end": v(9, 151.69) * mm});
            skArc(sketch, "E122.5", {"start": v(-11.93, 160.97) * mm, "mid": v(-11.27, 156.07) * mm, "end": v(-9, 151.69) * mm});
            skLineSegment(sketch, "E123", {"start": v(11.93, 159.83) * mm, "end": v(11.93, 177.8) * mm});
            skLineSegment(sketch, "E124", {"start": v(-11.93, 159.83) * mm, "end": v(-11.93, 177.8) * mm});
            skLineSegment(sketch, "E125", {"start": v(-7.87, 177.8) * mm, "end": v(-11.93, 177.8) * mm});
            skLineSegment(sketch, "E126", {"start": v(7.87, 177.8) * mm, "end": v(11.93, 177.8) * mm});
            skSolve(sketch);
        }
        {
            var Q0;
            Q0=makeQuery(id+"F47.imprint","IMPRINT",FACE,{"disambiguationData":[TD([[makeQuery(id+"F47.imprint","IMPRINT",EDGE,{"derivedFrom":sQuery(id+"F47.wireOp",EDGE,"E114")}),-1.0]])]});
            var Q1;
            Q1=makeQuery(id+"F8.opPattern","COPY",FACE,{"derivedFrom":makeQuery(id+"F1.opRevolve","SWEPT_FACE",FACE,{"disambiguationData":[OSD([sQuery(id+"F0.wireOp",EDGE,"E15")])]}),"instanceName":"1"});
            var Q2;
            Q2=makeQuery(id+"F1.opRevolve","SWEPT_FACE",FACE,{"disambiguationData":[OSD([sQuery(id+"F0.wireOp",EDGE,"E22")])]});
            extrude(context, id + "F48", {"entities" : qUnion([Q0]), "endBound" : BoundingType.UP_TO_SURFACE, "endBoundEntityFace" : qUnion([Q1]), "depth" : 25.4 * mm, "hasSecondDirection" : true, "secondDirectionBound" : SecondDirectionBoundingType.UP_TO_SURFACE, "secondDirectionOppositeDirection" : true, "secondDirectionBoundEntityFace" : qUnion([Q2]), "secondDirectionDepth" : 25.4 * mm});
        }
        {
            var Q0;
            Q0=makeQuery(id+"F48.opExtrude","SWEPT_FACE",FACE,{"disambiguationData":[OSD([sQuery(id+"F47.wireOp",EDGE,"E123")])]});
            var sketch = newSketch(context, id + "F49", { "sketchPlane" : qUnion([Q0])});
            skLineSegment(sketch, "E127", {"start": v(-97.98, 172.74) * mm, "end": v(-110.32, 177.33) * mm});
            skLineSegment(sketch, "E128", {"start": v(-110.32, 177.33) * mm, "end": v(-90.5, 169.96) * mm});
            skLineSegment(sketch, "E129", {"start": v(-90.5, 169.96) * mm, "end": v(-118.42, 180.34) * mm});
            skLineSegment(sketch, "E130", {"start": v(-118.42, 180.34) * mm, "end": v(-116.7, 184.99) * mm});
            skLineSegment(sketch, "E131", {"start": v(-116.7, 184.99) * mm, "end": v(-94.35, 182.99) * mm});
            skLineSegment(sketch, "E132", {"start": v(-94.35, 182.99) * mm, "end": v(-90.5, 169.96) * mm});
            skSolve(sketch);
        }
        {
            var Q0;
            {var subQ0=sQuery(id+"F49.wireOp",EDGE,"E130");Q0=makeQuery(id+"F49.imprint","IMPRINT",FACE,{"disambiguationData":[TD([[makeQuery(id+"F49.imprint","IMPRINT",EDGE,{"derivedFrom":subQ0}),-1.0]])]});}
            var Q1;
            {var subQ0=sQuery(id+"F49.wireOp",EDGE,"E129");var subQ10=makeQuery(id+"F49.imprint","IMPRINT",VERTEX,{"disambiguationData":[OD(0.0)],"derivedFrom":subQ0});Q1=makeQuery(id+"F49.imprint","IMPRINT",FACE,{"disambiguationData":[TD([[makeQuery(id+"F49.imprint","IMPRINT",EDGE,{"disambiguationData":[TD([[subQ10,-1.0]])],"derivedFrom":subQ0}),-1.0]])]});}
            extrude(context, id + "F50", {"entities" : qUnion([Q0, Q1]), "operationType" : NewBodyOperationType.REMOVE, "oppositeDirection" : true, "depth" : 5.08 * mm});
        }
        {
            var Q0;
            Q0=makeQuery(id+"F48.opExtrude","SWEPT_FACE",FACE,{"disambiguationData":[OSD([sQuery(id+"F47.wireOp",EDGE,"E123")])]});
            var sketch = newSketch(context, id + "F51", { "sketchPlane" : qUnion([Q0])});
            skArc(sketch, "E133", {"start": v(-110.32, 177.33) * mm, "mid": v(-113.6, 176.96) * mm, "end": v(-115.24, 174.1) * mm});
            skLineSegment(sketch, "E134", {"start": v(-110.32, 177.33) * mm, "end": v(-109.67, 179.08) * mm});
            skLineSegment(sketch, "E135", {"start": v(-109.67, 179.08) * mm, "end": v(-117.54, 181.05) * mm});
            skLineSegment(sketch, "E136", {"start": v(-115.24, 174.1) * mm, "end": v(-117.43, 174.1) * mm});
            skLineSegment(sketch, "E137", {"start": v(-117.43, 174.1) * mm, "end": v(-117.54, 181.05) * mm});
            skSolve(sketch);
        }
        {
            var Q0;
            {var subQ1=sQuery(id+"F51.wireOp",EDGE,"E134");Q0=makeQuery(id+"F51.imprint","IMPRINT",FACE,{"disambiguationData":[TD([[makeQuery(id+"F51.imprint","IMPRINT",EDGE,{"derivedFrom":subQ1}),1.0]])]});}
            var Q1;
            {var subQ0=sQuery(id+"F51.wireOp",EDGE,"E133");var subQ1=makeQuery(id+"F50.boolean.opBoolean","COPY",EDGE,{"derivedFrom":makeQuery(id+"F50.opExtrude","CAP_EDGE",EDGE,{"disambiguationData":[OSD([sQuery(id+"F49.wireOp",EDGE,"E129")])],"isStart":true})});var subQ2=makeQuery(id+"F51.imprint","INTERSECT",VERTEX,{"derivedFrom":[subQ1,subQ0]});Q1=makeQuery(id+"F51.imprint","IMPRINT",FACE,{"disambiguationData":[TD([[makeQuery(id+"F51.imprint","IMPRINT",EDGE,{"disambiguationData":[TD([[subQ2,-1.0]])],"derivedFrom":subQ0}),-1.0]])]});}
            extrude(context, id + "F52", {"entities" : qUnion([Q0, Q1]), "operationType" : NewBodyOperationType.REMOVE, "oppositeDirection" : true, "depth" : 5.08 * mm});
        }
        {
            var Q0;
            Q0=makeQuery(id+"F48.opExtrude","SWEPT_FACE",FACE,{"disambiguationData":[OSD([sQuery(id+"F47.wireOp",EDGE,"E123")])]});
            var sketch = newSketch(context, id + "F53", { "sketchPlane" : qUnion([Q0])});
            skArc(sketch, "E138", {"start": v(-94.26, 167.77) * mm, "mid": v(-95.38, 170.8) * mm, "end": v(-97.98, 172.74) * mm});
            skLineSegment(sketch, "E139", {"start": v(-97.98, 172.74) * mm, "end": v(-96.3, 175.92) * mm});
            skLineSegment(sketch, "E140", {"start": v(-96.3, 175.92) * mm, "end": v(-88.68, 171.9) * mm});
            skLineSegment(sketch, "E141", {"start": v(-88.68, 171.9) * mm, "end": v(-92.08, 166.46) * mm});
            skLineSegment(sketch, "E142", {"start": v(-94.26, 167.77) * mm, "end": v(-92.5, 166.84) * mm});
            skLineSegment(sketch, "E143", {"start": v(-92.5, 166.84) * mm, "end": v(-92.08, 166.46) * mm});
            skSolve(sketch);
        }
        {
            var Q0;
            {var subQ0=sQuery(id+"F53.wireOp",EDGE,"E138");var subQ1=makeQuery(id+"F50.boolean.opBoolean","COPY",EDGE,{"derivedFrom":makeQuery(id+"F50.opExtrude","CAP_EDGE",EDGE,{"disambiguationData":[OSD([sQuery(id+"F49.wireOp",EDGE,"E129")])],"isStart":true})});var subQ2=makeQuery(id+"F53.imprint","INTERSECT",VERTEX,{"derivedFrom":[subQ1,subQ0]});Q0=makeQuery(id+"F53.imprint","IMPRINT",FACE,{"disambiguationData":[TD([[makeQuery(id+"F53.imprint","IMPRINT",EDGE,{"disambiguationData":[TD([[subQ2,1.0]])],"derivedFrom":subQ1}),1.0]])]});}
            var Q1;
            {var subQ0=sQuery(id+"F53.wireOp",EDGE,"E139");Q1=makeQuery(id+"F53.imprint","IMPRINT",FACE,{"disambiguationData":[TD([[makeQuery(id+"F53.imprint","IMPRINT",EDGE,{"derivedFrom":subQ0}),-1.0]])]});}
            extrude(context, id + "F54", {"entities" : qUnion([Q0, Q1]), "operationType" : NewBodyOperationType.REMOVE, "oppositeDirection" : true, "depth" : 5.08 * mm});
        }
        {
            var Q0;
            Q0=makeQuery(id+"F48.opExtrude","SWEPT_FACE",FACE,{"disambiguationData":[OSD([sQuery(id+"F47.wireOp",EDGE,"E124")])]});
            var sketch = newSketch(context, id + "F55", { "sketchPlane" : qUnion([Q0])});
            skLineSegment(sketch, "E144", {"start": v(110.32, 177.33) * mm, "end": v(97.98, 172.74) * mm});
            skLineSegment(sketch, "E145", {"start": v(97.98, 172.74) * mm, "end": v(120.99, 181.3) * mm});
            skLineSegment(sketch, "E146", {"start": v(120.99, 181.3) * mm, "end": v(87.56, 168.87) * mm});
            skLineSegment(sketch, "E147", {"start": v(87.56, 168.87) * mm, "end": v(87.36, 169.4) * mm});
            skLineSegment(sketch, "E148", {"start": v(87.36, 169.4) * mm, "end": v(87.56, 182.32) * mm});
            skLineSegment(sketch, "E149", {"start": v(87.56, 182.32) * mm, "end": v(120.99, 181.3) * mm});
            skSolve(sketch);
        }
        {
            var Q0;
            {var subQ0=sQuery(id+"F55.wireOp",EDGE,"E147");Q0=makeQuery(id+"F55.imprint","IMPRINT",FACE,{"disambiguationData":[TD([[makeQuery(id+"F55.imprint","IMPRINT",EDGE,{"derivedFrom":subQ0}),-1.0]])]});}
            var Q1;
            {var subQ0=sQuery(id+"F55.wireOp",EDGE,"E146");var subQ10=makeQuery(id+"F55.imprint","IMPRINT",VERTEX,{"disambiguationData":[OD(0.0)],"derivedFrom":subQ0});Q1=makeQuery(id+"F55.imprint","IMPRINT",FACE,{"disambiguationData":[TD([[makeQuery(id+"F55.imprint","IMPRINT",EDGE,{"disambiguationData":[TD([[subQ10,-1.0]])],"derivedFrom":subQ0}),-1.0]])]});}
            extrude(context, id + "F56", {"entities" : qUnion([Q0, Q1]), "operationType" : NewBodyOperationType.REMOVE, "oppositeDirection" : true, "depth" : 5.08 * mm});
        }
        {
            var Q0;
            Q0=makeQuery(id+"F48.opExtrude","SWEPT_FACE",FACE,{"disambiguationData":[OSD([sQuery(id+"F47.wireOp",EDGE,"E124")])]});
            var sketch = newSketch(context, id + "F57", { "sketchPlane" : qUnion([Q0])});
            skArc(sketch, "E150", {"start": v(115.24, 174.1) * mm, "mid": v(113.6, 176.96) * mm, "end": v(110.32, 177.33) * mm});
            skLineSegment(sketch, "E151", {"start": v(115.24, 174.1) * mm, "end": v(120.55, 174.1) * mm});
            skLineSegment(sketch, "E152", {"start": v(120.55, 174.1) * mm, "end": v(120.07, 180.05) * mm});
            skLineSegment(sketch, "E153", {"start": v(120.07, 180.05) * mm, "end": v(110.52, 180.05) * mm});
            skLineSegment(sketch, "E154", {"start": v(110.52, 180.05) * mm, "end": v(110.32, 177.33) * mm});
            skSolve(sketch);
        }
        {
            var Q0;
            {var subQ0=sQuery(id+"F57.wireOp",EDGE,"E150");var subQ1=makeQuery(id+"F56.boolean.opBoolean","COPY",EDGE,{"derivedFrom":makeQuery(id+"F56.opExtrude","CAP_EDGE",EDGE,{"disambiguationData":[OSD([sQuery(id+"F55.wireOp",EDGE,"E146")])],"isStart":true})});var subQ2=makeQuery(id+"F57.imprint","INTERSECT",VERTEX,{"derivedFrom":[subQ1,subQ0]});Q0=makeQuery(id+"F57.imprint","IMPRINT",FACE,{"disambiguationData":[TD([[makeQuery(id+"F57.imprint","IMPRINT",EDGE,{"disambiguationData":[TD([[subQ2,1.0]])],"derivedFrom":subQ0}),-1.0]])]});}
            var Q1;
            {var subQ0=sQuery(id+"F57.wireOp",EDGE,"E151");Q1=makeQuery(id+"F57.imprint","IMPRINT",FACE,{"disambiguationData":[TD([[makeQuery(id+"F57.imprint","IMPRINT",EDGE,{"derivedFrom":subQ0}),1.0]])]});}
            extrude(context, id + "F58", {"entities" : qUnion([Q0, Q1]), "operationType" : NewBodyOperationType.REMOVE, "oppositeDirection" : true, "depth" : 5.08 * mm});
        }
        {
            var Q0;
            Q0=makeQuery(id+"F48.opExtrude","SWEPT_FACE",FACE,{"disambiguationData":[OSD([sQuery(id+"F47.wireOp",EDGE,"E124")])]});
            var sketch = newSketch(context, id + "F59", { "sketchPlane" : qUnion([Q0])});
            skArc(sketch, "E155", {"start": v(97.98, 172.74) * mm, "mid": v(95.38, 170.8) * mm, "end": v(94.26, 167.77) * mm});
            skLineSegment(sketch, "E156", {"start": v(94.26, 167.77) * mm, "end": v(90.1, 167.77) * mm});
            skLineSegment(sketch, "E157", {"start": v(90.1, 167.77) * mm, "end": v(89.2, 176.46) * mm});
            skLineSegment(sketch, "E158", {"start": v(89.2, 176.46) * mm, "end": v(98.03, 178.16) * mm});
            skLineSegment(sketch, "E159", {"start": v(98.03, 178.16) * mm, "end": v(97.98, 172.74) * mm});
            skSolve(sketch);
        }
        {
            var Q0;
            {var subQ0=sQuery(id+"F59.wireOp",EDGE,"E155");var subQ1=makeQuery(id+"F56.boolean.opBoolean","COPY",EDGE,{"derivedFrom":makeQuery(id+"F56.opExtrude","CAP_EDGE",EDGE,{"disambiguationData":[OSD([sQuery(id+"F55.wireOp",EDGE,"E146")])],"isStart":true})});var subQ2=makeQuery(id+"F59.imprint","INTERSECT",VERTEX,{"derivedFrom":[subQ1,subQ0]});Q0=makeQuery(id+"F59.imprint","IMPRINT",FACE,{"disambiguationData":[TD([[makeQuery(id+"F59.imprint","IMPRINT",EDGE,{"disambiguationData":[TD([[subQ2,-1.0]])],"derivedFrom":subQ1}),1.0]])]});}
            var Q1;
            {var subQ0=sQuery(id+"F59.wireOp",EDGE,"E156");Q1=makeQuery(id+"F59.imprint","IMPRINT",FACE,{"disambiguationData":[TD([[makeQuery(id+"F59.imprint","IMPRINT",EDGE,{"derivedFrom":subQ0}),-1.0]])]});}
            extrude(context, id + "F60", {"entities" : qUnion([Q0, Q1]), "operationType" : NewBodyOperationType.REMOVE, "oppositeDirection" : true, "depth" : 5.08 * mm});
        }
        {
            var Q0;
            Q0=makeQuery(id+"F14.opPattern","COPY",FACE,{"derivedFrom":makeQuery(id+"F3.opExtrude","CAP_FACE",FACE,{"disambiguationData":[OSD([sQuery(id+"F2.wireOp",EDGE,"E45"),sQuery(id+"F2.wireOp",EDGE,"E47"),sQuery(id+"F2.wireOp",EDGE,"E48"),sQuery(id+"F2.wireOp",EDGE,"E49"),sQuery(id+"F2.wireOp",EDGE,"E50"),sQuery(id+"F2.wireOp",EDGE,"E51")])],"isStart":false}),"instanceName":"1"});
            cPlane(context, id + "F61", {"entities" : qUnion([Q0]), "cplaneType" : CPlaneType.OFFSET, "offset" : 0 * mm, "width" : 152.4 * mm, "height" : 152.4 * mm});
        }
        {
            var Q0;
            Q0=makeQuery(id+"F14.opPattern","COPY",FACE,{"derivedFrom":makeQuery(id+"F3.opExtrude","CAP_FACE",FACE,{"disambiguationData":[OSD([sQuery(id+"F2.wireOp",EDGE,"E45"),sQuery(id+"F2.wireOp",EDGE,"E47"),sQuery(id+"F2.wireOp",EDGE,"E48"),sQuery(id+"F2.wireOp",EDGE,"E49"),sQuery(id+"F2.wireOp",EDGE,"E50"),sQuery(id+"F2.wireOp",EDGE,"E51")])],"isStart":true}),"instanceName":"1"});
            cPlane(context, id + "F62", {"entities" : qUnion([Q0]), "cplaneType" : CPlaneType.OFFSET, "offset" : 0 * mm, "width" : 152.4 * mm, "height" : 152.4 * mm});
        }
        {
            var Q0;
            Q0=qCreatedBy(id+"F62.planeOp",FACE);
            var Q1;
            Q1=qCreatedBy(id+"F61.planeOp",FACE);
            cPlane(context, id + "F63", {"entities" : qUnion([Q0, Q1]), "cplaneType" : CPlaneType.MID_PLANE, "offset" : 25.4 * mm, "width" : 152.4 * mm, "height" : 152.4 * mm});
        }
        {
            var Q0;
            Q0=qCreatedBy(id+"F63.planeOp",FACE);
            var sketch = newSketch(context, id + "F64", { "sketchPlane" : qUnion([Q0])});
            skLineSegment(sketch, "E160", {"start": v(115.62, 140.97) * mm, "end": v(125.02, 140.97) * mm, "construction": true});
            skLineSegment(sketch, "E161", {"start": v(115.62, 140.97) * mm, "end": v(120.32, 140.97) * mm, "construction": true});
            skLineSegment(sketch, "E162", {"start": v(116.92, 151.12) * mm, "end": v(115.15, 151.12) * mm});
            skLineSegment(sketch, "E163", {"start": v(115.15, 151.12) * mm, "end": v(115.44, 144.83) * mm});
            skLineSegment(sketch, "E164", {"start": v(53.49, 211.36) * mm, "end": v(53.49, 211.36) * mm});
            skArc(sketch, "E165", {"start": v(115.44, 144.83) * mm, "mid": v(120.23, 140.04) * mm, "end": v(125.02, 144.83) * mm});
            skLineSegment(sketch, "E166", {"start": v(125.02, 152.45) * mm, "end": v(123.75, 152.45) * mm});
            skLineSegment(sketch, "E167", {"start": v(123.75, 152.45) * mm, "end": v(123.24, 144.83) * mm});
            skLineSegment(sketch, "E168", {"start": v(120.23, 140.97) * mm, "end": v(120.23, 141.82) * mm});
            skArc(sketch, "E169", {"start": v(117.22, 144.83) * mm, "mid": v(120.23, 141.82) * mm, "end": v(123.24, 144.83) * mm});
            skLineSegment(sketch, "E170", {"start": v(116.92, 151.12) * mm, "end": v(117.22, 144.83) * mm});
            skPoint(sketch, "E171.orphan", {"position": v(120.23, 140.04) * mm});
            skLineSegment(sketch, "E172", {"start": v(125.02, 152.45) * mm, "end": v(125.02, 144.83) * mm});
            skLineSegment(sketch, "E173", {"start": v(0, 0) * mm, "end": v(0, 224.67) * mm, "construction": true});
            skLineSegment(sketch, "E174", {"start": v(115.44, 144.83) * mm, "end": v(0, 144.83) * mm, "construction": true});
            skLineSegment(sketch, "E175", {"start": v(0, 144.83) * mm, "end": v(-115.44, 144.83) * mm, "construction": true});
            skLineSegment(sketch, "E176.MirrorCS", {"start": v(-115.15, 151.12) * mm, "end": v(-115.44, 144.83) * mm});
            skLineSegment(sketch, "E177.MirrorCS", {"start": v(-116.92, 151.12) * mm, "end": v(-115.15, 151.12) * mm});
            skLineSegment(sketch, "E178.MirrorCS", {"start": v(-116.92, 151.12) * mm, "end": v(-117.22, 144.83) * mm});
            skArc(sketch, "E179.MirrorCS", {"start": v(-117.22, 144.83) * mm, "mid": v(-120.23, 141.82) * mm, "end": v(-123.24, 144.83) * mm});
            skLineSegment(sketch, "E180.MirrorCS", {"start": v(-123.75, 152.45) * mm, "end": v(-123.24, 144.83) * mm});
            skLineSegment(sketch, "E181.MirrorCS", {"start": v(-125.02, 152.45) * mm, "end": v(-123.75, 152.45) * mm});
            skLineSegment(sketch, "E182.MirrorCS", {"start": v(-125.02, 152.45) * mm, "end": v(-125.02, 144.83) * mm});
            skArc(sketch, "E183.MirrorCS", {"start": v(-115.44, 144.83) * mm, "mid": v(-120.23, 140.04) * mm, "end": v(-125.02, 144.83) * mm});
            skSolve(sketch);
        }
        {
            var Q0;
            Q0=makeQuery(id+"F64.imprint","IMPRINT",FACE,{"disambiguationData":[TD([[makeQuery(id+"F64.imprint","IMPRINT",EDGE,{"derivedFrom":sQuery(id+"F64.wireOp",EDGE,"E176.MirrorCS")}),-1.0]])]});
            var Q1;
            Q1=sQuery(id+"F64.wireOp",EDGE,"E173");
            revolve(context, id + "F65", {"entities" : qUnion([Q0]), "axis" : qUnion([Q1]), "revolveType" : RevolveType.SYMMETRIC, "angle" : 6 * degree});
        }
        {
            var Q0;
            Q0=makeQuery(id+"F65.opRevolve","CAP_EDGE",EDGE,{"disambiguationData":[OSD([sQuery(id+"F64.wireOp",EDGE,"E181.MirrorCS")])],"isStart":true});
            var Q1;
            Q1=makeQuery(id+"F65.opRevolve","CAP_EDGE",EDGE,{"disambiguationData":[OSD([sQuery(id+"F64.wireOp",EDGE,"E181.MirrorCS")])],"isStart":false});
            fillet(context, id + "F66", {"entities" : qUnion([Q0, Q1]), "radius" : 6.35 * mm, "tangentPropagation" : true, "allowEdgeOverflow" : false});
        }
    });
